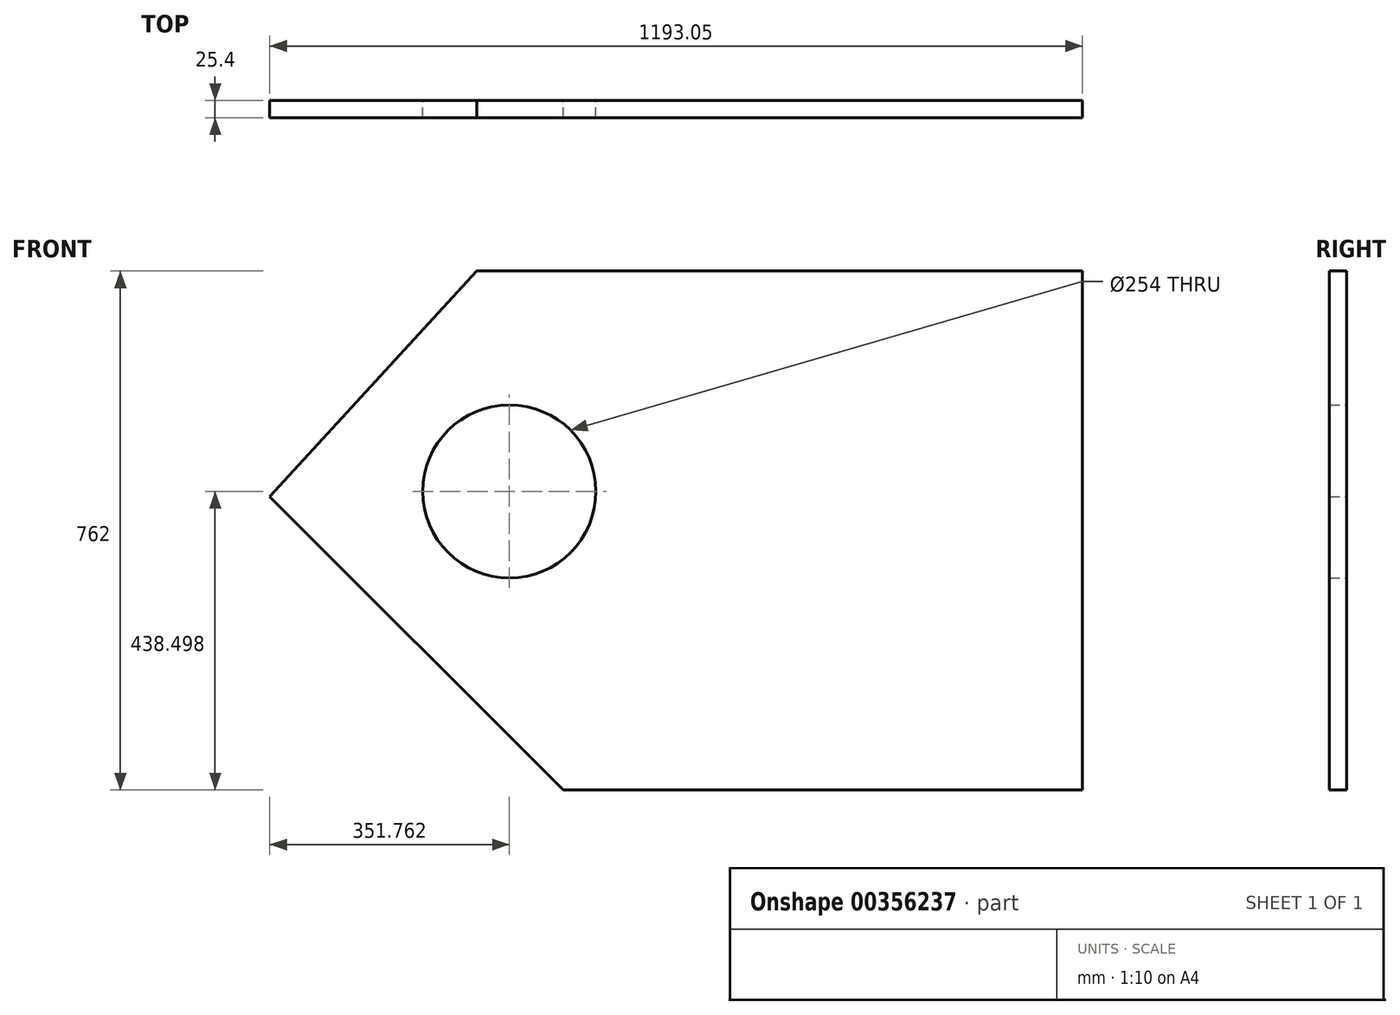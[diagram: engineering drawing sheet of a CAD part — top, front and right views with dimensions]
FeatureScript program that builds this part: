
annotation { "Feature Type Name" : "Feature", "Feature Type Description" : "" }
export const myFeature = defineFeature(function(context is Context, id is Id, definition is map)
    precondition{}
    {
        {
            var Q0;
            Q0=qCreatedBy(makeId("Front.planeOp"),FACE);
            var sketch = newSketch(context, id + "F0", { "sketchPlane" : qUnion([Q0])});
            skLineSegment(sketch, "E0", {"start": v(0, 0) * mm, "end": v(762, 0) * mm});
            skLineSegment(sketch, "E1", {"start": v(762, 0) * mm, "end": v(762, 762) * mm});
            skLineSegment(sketch, "E2", {"start": v(762, 762) * mm, "end": v(-127, 762) * mm});
            skLineSegment(sketch, "E3", {"start": v(-127, 762) * mm, "end": v(-431.05, 431.05) * mm});
            skLineSegment(sketch, "E4", {"start": v(-431.05, 431.05) * mm, "end": v(0, 0) * mm});
            skCircle(sketch, "E5", {"center": v(-79.29, 438.5) * mm, "radius": 127 * mm});
            skSolve(sketch);
        }
        {
            var Q0;
            Q0 = qSketchRegion(id + "F0", true);
            extrude(context, id + "F1", {"entities" : qUnion([Q0]), "depth" : 25.4 * mm});
        }
    });
